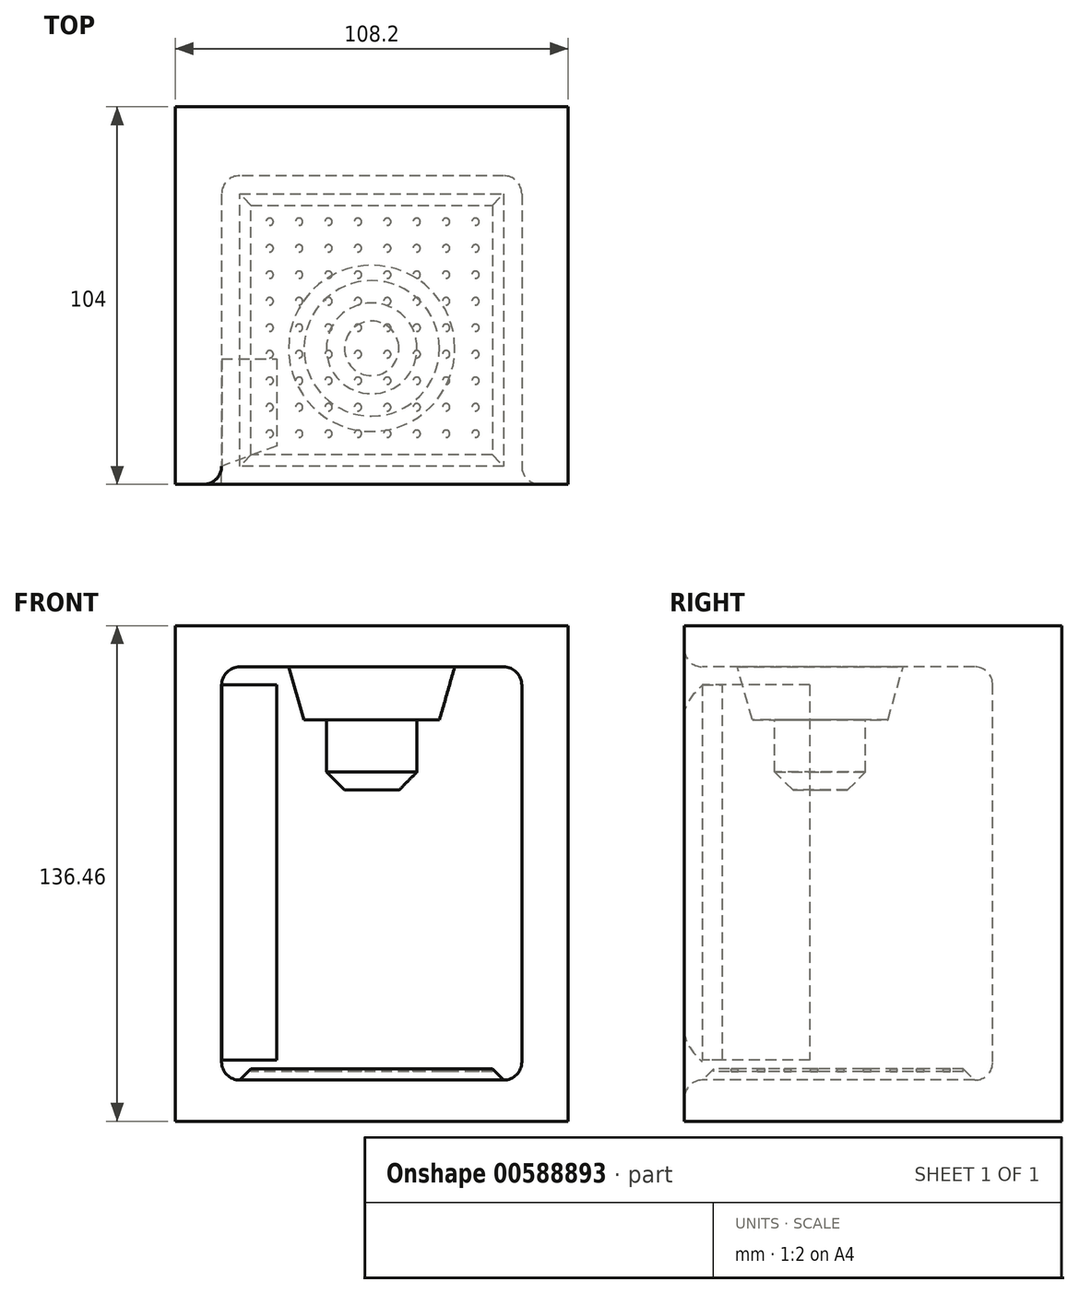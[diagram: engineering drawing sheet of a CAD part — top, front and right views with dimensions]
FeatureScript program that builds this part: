
annotation { "Feature Type Name" : "Feature", "Feature Type Description" : "" }
export const myFeature = defineFeature(function(context is Context, id is Id, definition is map)
    precondition{}
    {
        {
            var Q0;
            Q0=qCreatedBy(makeId("Front.planeOp"),FACE);
            var sketch = newSketch(context, id + "F0", { "sketchPlane" : qUnion([Q0])});
            skLineSegment(sketch, "E0.bottom", {"start": v(54.1, -68.23) * mm, "end": v(-54.1, -68.23) * mm});
            skLineSegment(sketch, "E0.top", {"start": v(54.1, 68.23) * mm, "end": v(-54.1, 68.23) * mm});
            skLineSegment(sketch, "E0.left", {"start": v(54.1, -68.23) * mm, "end": v(54.1, 68.23) * mm});
            skLineSegment(sketch, "E0.right", {"start": v(-54.1, -68.23) * mm, "end": v(-54.1, 68.23) * mm});
            skPoint(sketch, "E0.middle", {"position": v(0, 0) * mm});
            skSolve(sketch);
        }
        {
            var Q0;
            Q0=makeQuery(id+"F0.imprint","IMPRINT",FACE,{"disambiguationData":[TD([[makeQuery(id+"F0.imprint","IMPRINT",EDGE,{"derivedFrom":sQuery(id+"F0.wireOp",EDGE,"E0.bottom")}),-1.0]])]});
            extrude(context, id + "F1", {"entities" : qUnion([Q0]), "depth" : 104 * mm, "offsetDistance" : 25 * mm, "symmetric" : true});
        }
        {
            var Q0;
            Q0=makeQuery(id+"F1.opExtrude","CAP_FACE",FACE,{"disambiguationData":[OSD([sQuery(id+"F0.wireOp",EDGE,"E0.bottom"),sQuery(id+"F0.wireOp",EDGE,"E0.top"),sQuery(id+"F0.wireOp",EDGE,"E0.left"),sQuery(id+"F0.wireOp",EDGE,"E0.right")])],"isStart":false});
            var sketch = newSketch(context, id + "F2", { "sketchPlane" : qUnion([Q0])});
            skLineSegment(sketch, "E1.bottom", {"start": v(41.35, -56.91) * mm, "end": v(-41.35, -56.91) * mm});
            skLineSegment(sketch, "E1.top", {"start": v(41.35, 56.91) * mm, "end": v(-41.35, 56.91) * mm});
            skLineSegment(sketch, "E1.left", {"start": v(41.35, -56.91) * mm, "end": v(41.35, 56.91) * mm});
            skLineSegment(sketch, "E1.right", {"start": v(-41.35, -56.91) * mm, "end": v(-41.35, 56.91) * mm});
            skPoint(sketch, "E1.middle", {"position": v(0, 0) * mm});
            skSolve(sketch);
        }
        {
            var Q0;
            Q0=makeQuery(id+"F2.imprint","IMPRINT",FACE,{"disambiguationData":[TD([[makeQuery(id+"F2.imprint","IMPRINT",EDGE,{"derivedFrom":sQuery(id+"F2.wireOp",EDGE,"E1.bottom")}),-1.0]])]});
            extrude(context, id + "F3", {"entities" : qUnion([Q0]), "operationType" : NewBodyOperationType.REMOVE, "oppositeDirection" : true, "depth" : 85 * mm, "offsetDistance" : 25 * mm});
        }
        {
            var Q0;
            Q0=makeQuery(id+"F3.boolean.opBoolean","COPY",FACE,{"derivedFrom":makeQuery(id+"F3.opExtrude","SWEPT_FACE",FACE,{"disambiguationData":[OSD([sQuery(id+"F2.wireOp",EDGE,"E1.top")])]})});
            var Q1;
            Q1=makeQuery(id+"F3.boolean.opBoolean","COPY",FACE,{"derivedFrom":makeQuery(id+"F3.opExtrude","SWEPT_FACE",FACE,{"disambiguationData":[OSD([sQuery(id+"F2.wireOp",EDGE,"E1.bottom")])]})});
            var Q2;
            Q2=makeQuery(id+"F3.boolean.opBoolean","COPY",FACE,{"derivedFrom":makeQuery(id+"F3.opExtrude","SWEPT_FACE",FACE,{"disambiguationData":[OSD([sQuery(id+"F2.wireOp",EDGE,"E1.left")])]})});
            var Q3;
            Q3=makeQuery(id+"F3.boolean.opBoolean","COPY",FACE,{"derivedFrom":makeQuery(id+"F3.opExtrude","CAP_FACE",FACE,{"disambiguationData":[OSD([sQuery(id+"F2.wireOp",EDGE,"E1.bottom"),sQuery(id+"F2.wireOp",EDGE,"E1.top"),sQuery(id+"F2.wireOp",EDGE,"E1.left"),sQuery(id+"F2.wireOp",EDGE,"E1.right")])],"isStart":false})});
            fillet(context, id + "F4", {"entities" : qUnion([Q0, Q1, Q2, Q3]), "radius" : 5 * mm, "tangentPropagation" : true, "allowEdgeOverflow" : false});
        }
        {
            var Q0;
            Q0=qCreatedBy(makeId("Right.planeOp"),FACE);
            var sketch = newSketch(context, id + "F5", { "sketchPlane" : qUnion([Q0])});
            skLineSegment(sketch, "E2", {"start": v(-14.56, 56.98) * mm, "end": v(-14.56, 35.68) * mm});
            skLineSegment(sketch, "E3", {"start": v(-14.56, 35.68) * mm, "end": v(-2.06, 35.68) * mm});
            skLineSegment(sketch, "E4", {"start": v(-2.06, 35.68) * mm, "end": v(-2.06, 42.37) * mm});
            skLineSegment(sketch, "E5", {"start": v(-2.06, 42.37) * mm, "end": v(4.1, 42.37) * mm});
            skLineSegment(sketch, "E6", {"start": v(4.1, 42.37) * mm, "end": v(8.33, 56.98) * mm});
            skLineSegment(sketch, "E7", {"start": v(8.33, 56.98) * mm, "end": v(-14.56, 56.98) * mm});
            skSolve(sketch);
        }
        {
            var Q0;
            Q0=makeQuery(id+"F5.imprint","IMPRINT",FACE,{"disambiguationData":[TD([[makeQuery(id+"F5.imprint","IMPRINT",EDGE,{"derivedFrom":sQuery(id+"F5.wireOp",EDGE,"E2")}),1.0]])]});
            var Q1;
            Q1=sQuery(id+"F5.wireOp",EDGE,"E2");
            revolve(context, id + "F6", {"entities" : qUnion([Q0]), "axis" : qUnion([Q1]), "revolveType" : RevolveType.FULL});
        }
        {
            var Q0;
            Q0=qCreatedBy(makeId("Front.planeOp"),FACE);
            cPlane(context, id + "F7", {"entities" : qUnion([Q0]), "cplaneType" : CPlaneType.OFFSET, "offset" : 47 * mm, "width" : 150 * mm, "height" : 150 * mm});
        }
        {
            var Q0;
            Q0=qCreatedBy(id+"F7.planeOp",FACE);
            var sketch = newSketch(context, id + "F8", { "sketchPlane" : qUnion([Q0])});
            skLineSegment(sketch, "E8.bottom", {"start": v(-41.3, 51.96) * mm, "end": v(-26.2, 51.96) * mm});
            skLineSegment(sketch, "E8.top", {"start": v(-41.3, -51.37) * mm, "end": v(-26.2, -51.37) * mm});
            skLineSegment(sketch, "E8.left", {"start": v(-41.3, 51.96) * mm, "end": v(-41.3, -51.37) * mm});
            skLineSegment(sketch, "E8.right", {"start": v(-26.2, 51.96) * mm, "end": v(-26.2, -51.37) * mm});
            skSolve(sketch);
        }
        {
            var Q0;
            Q0=makeQuery(id+"F8.imprint","IMPRINT",FACE,{"disambiguationData":[TD([[makeQuery(id+"F8.imprint","IMPRINT",EDGE,{"derivedFrom":sQuery(id+"F8.wireOp",EDGE,"E8.bottom")}),-1.0]])]});
            extrude(context, id + "F9", {"entities" : qUnion([Q0]), "oppositeDirection" : true, "depth" : 29.6 * mm, "offsetDistance" : 25 * mm});
        }
        {
            var Q0;
            Q0=makeQuery(id+"F9.opExtrude","SWEPT_FACE",FACE,{"disambiguationData":[OSD([sQuery(id+"F8.wireOp",EDGE,"E8.bottom")])]});
            var sketch = newSketch(context, id + "F10", { "sketchPlane" : qUnion([Q0])});
            skLineSegment(sketch, "E9", {"start": v(-41.3, -47) * mm, "end": v(-23.88, -40.54) * mm});
            skLineSegment(sketch, "E10", {"start": v(-23.88, -40.54) * mm, "end": v(-23.88, -62.45) * mm});
            skLineSegment(sketch, "E11", {"start": v(-23.88, -62.45) * mm, "end": v(-41.3, -47) * mm});
            skSolve(sketch);
        }
        {
            var Q0;
            {var subQ1=sQuery(id+"F8.wireOp",EDGE,"E8.bottom");var subQ2=makeQuery(id+"F9.opExtrude","CAP_EDGE",EDGE,{"disambiguationData":[OSD([subQ1])],"isStart":true});Q0=makeQuery(id+"F10.imprint","IMPRINT",FACE,{"disambiguationData":[TD([[makeQuery(id+"F10.imprint","IMPRINT",EDGE,{"derivedFrom":subQ2}),1.0]])]});}
            extrude(context, id + "F11", {"entities" : qUnion([Q0]), "operationType" : NewBodyOperationType.REMOVE, "oppositeDirection" : true, "depth" : 104.4 * mm, "offsetDistance" : 25 * mm});
        }
        {
            var Q0;
            Q0=makeQuery(id+"F6.opRevolve","SWEPT_FACE",FACE,{"disambiguationData":[OSD([sQuery(id+"F5.wireOp",EDGE,"E3")])]});
            extrude(context, id + "F12", {"entities" : qUnion([Q0]), "operationType" : NewBodyOperationType.ADD, "depth" : 12.7 * mm, "offsetDistance" : 25 * mm});
        }
        {
            var Q0;
            Q0=makeQuery(id+"F12.opExtrude","CAP_EDGE",EDGE,{"disambiguationData":[OSD([sQuery(id+"F5.wireOp",EDGE,"E3"),sQuery(id+"F5.wireOp",EDGE,"E4")])],"isStart":false});
            chamfer(context, id + "F13", {"entities" : qUnion([Q0]), "width" : 5 * mm, "tangentPropagation" : true});
        }
        {
            var Q0;
            Q0=makeQuery(id+"F3.boolean.opBoolean","COPY",FACE,{"derivedFrom":makeQuery(id+"F3.opExtrude","SWEPT_FACE",FACE,{"disambiguationData":[OSD([sQuery(id+"F2.wireOp",EDGE,"E1.bottom")])]})});
            extrude(context, id + "F14", {"entities" : qUnion([Q0]), "depth" : 3.1 * mm, "offsetDistance" : 25 * mm, "hasDraft" : true, "draftAngle" : 45 * degree, "draftPullDirection" : true});
        }
        {
            var Q0;
            Q0=makeQuery(id+"F14.opExtrude","CAP_FACE",FACE,{"disambiguationData":[OSD([sQuery(id+"F2.wireOp",EDGE,"E1.bottom")])],"isStart":false});
            var sketch = newSketch(context, id + "F15", { "sketchPlane" : qUnion([Q0])});
            skCircle(sketch, "E12", {"center": v(-28.1, 20.32) * mm, "radius": 1 * mm});
            skCircle(sketch, "E13.0.1.0", {"center": v(-28.1, 13.02) * mm, "radius": 1 * mm});
            skCircle(sketch, "E13.0.2.0", {"center": v(-28.1, 5.72) * mm, "radius": 1 * mm});
            skCircle(sketch, "E13.0.3.0", {"center": v(-28.1, -1.58) * mm, "radius": 1 * mm});
            skCircle(sketch, "E13.0.4.0", {"center": v(-28.1, -8.88) * mm, "radius": 1 * mm});
            skCircle(sketch, "E13.0.5.0", {"center": v(-28.1, -16.18) * mm, "radius": 1 * mm});
            skCircle(sketch, "E13.0.6.0", {"center": v(-28.1, -23.48) * mm, "radius": 1 * mm});
            skCircle(sketch, "E13.0.7.0", {"center": v(-28.1, -30.78) * mm, "radius": 1 * mm});
            skCircle(sketch, "E13.0.8.0", {"center": v(-28.1, -38.08) * mm, "radius": 1 * mm});
            skCircle(sketch, "E13.1.0.0", {"center": v(-20, 20.32) * mm, "radius": 1 * mm});
            skCircle(sketch, "E13.1.1.0", {"center": v(-20, 13.02) * mm, "radius": 1 * mm});
            skCircle(sketch, "E13.1.2.0", {"center": v(-20, 5.72) * mm, "radius": 1 * mm});
            skCircle(sketch, "E13.1.3.0", {"center": v(-20, -1.58) * mm, "radius": 1 * mm});
            skCircle(sketch, "E13.1.4.0", {"center": v(-20, -8.88) * mm, "radius": 1 * mm});
            skCircle(sketch, "E13.1.5.0", {"center": v(-20, -16.18) * mm, "radius": 1 * mm});
            skCircle(sketch, "E13.1.6.0", {"center": v(-20, -23.48) * mm, "radius": 1 * mm});
            skCircle(sketch, "E13.1.7.0", {"center": v(-20, -30.78) * mm, "radius": 1 * mm});
            skCircle(sketch, "E13.1.8.0", {"center": v(-20, -38.08) * mm, "radius": 1 * mm});
            skCircle(sketch, "E13.2.0.0", {"center": v(-11.9, 20.32) * mm, "radius": 1 * mm});
            skCircle(sketch, "E13.2.1.0", {"center": v(-11.9, 13.02) * mm, "radius": 1 * mm});
            skCircle(sketch, "E13.2.2.0", {"center": v(-11.9, 5.72) * mm, "radius": 1 * mm});
            skCircle(sketch, "E13.2.3.0", {"center": v(-11.9, -1.58) * mm, "radius": 1 * mm});
            skCircle(sketch, "E13.2.4.0", {"center": v(-11.9, -8.88) * mm, "radius": 1 * mm});
            skCircle(sketch, "E13.2.5.0", {"center": v(-11.9, -16.18) * mm, "radius": 1 * mm});
            skCircle(sketch, "E13.2.6.0", {"center": v(-11.9, -23.48) * mm, "radius": 1 * mm});
            skCircle(sketch, "E13.2.7.0", {"center": v(-11.9, -30.78) * mm, "radius": 1 * mm});
            skCircle(sketch, "E13.2.8.0", {"center": v(-11.9, -38.08) * mm, "radius": 1 * mm});
            skCircle(sketch, "E13.3.0.0", {"center": v(-3.8, 20.32) * mm, "radius": 1 * mm});
            skCircle(sketch, "E13.3.1.0", {"center": v(-3.8, 13.02) * mm, "radius": 1 * mm});
            skCircle(sketch, "E13.3.2.0", {"center": v(-3.8, 5.72) * mm, "radius": 1 * mm});
            skCircle(sketch, "E13.3.3.0", {"center": v(-3.8, -1.58) * mm, "radius": 1 * mm});
            skCircle(sketch, "E13.3.4.0", {"center": v(-3.8, -8.88) * mm, "radius": 1 * mm});
            skCircle(sketch, "E13.3.5.0", {"center": v(-3.8, -16.18) * mm, "radius": 1 * mm});
            skCircle(sketch, "E13.3.6.0", {"center": v(-3.8, -23.48) * mm, "radius": 1 * mm});
            skCircle(sketch, "E13.3.7.0", {"center": v(-3.8, -30.78) * mm, "radius": 1 * mm});
            skCircle(sketch, "E13.3.8.0", {"center": v(-3.8, -38.08) * mm, "radius": 1 * mm});
            skCircle(sketch, "E13.4.0.0", {"center": v(4.3, 20.32) * mm, "radius": 1 * mm});
            skCircle(sketch, "E13.4.1.0", {"center": v(4.3, 13.02) * mm, "radius": 1 * mm});
            skCircle(sketch, "E13.4.2.0", {"center": v(4.3, 5.72) * mm, "radius": 1 * mm});
            skCircle(sketch, "E13.4.3.0", {"center": v(4.3, -1.58) * mm, "radius": 1 * mm});
            skCircle(sketch, "E13.4.4.0", {"center": v(4.3, -8.88) * mm, "radius": 1 * mm});
            skCircle(sketch, "E13.4.5.0", {"center": v(4.3, -16.18) * mm, "radius": 1 * mm});
            skCircle(sketch, "E13.4.6.0", {"center": v(4.3, -23.48) * mm, "radius": 1 * mm});
            skCircle(sketch, "E13.4.7.0", {"center": v(4.3, -30.78) * mm, "radius": 1 * mm});
            skCircle(sketch, "E13.4.8.0", {"center": v(4.3, -38.08) * mm, "radius": 1 * mm});
            skCircle(sketch, "E13.5.0.0", {"center": v(12.4, 20.32) * mm, "radius": 1 * mm});
            skCircle(sketch, "E13.5.1.0", {"center": v(12.4, 13.02) * mm, "radius": 1 * mm});
            skCircle(sketch, "E13.5.2.0", {"center": v(12.4, 5.72) * mm, "radius": 1 * mm});
            skCircle(sketch, "E13.5.3.0", {"center": v(12.4, -1.58) * mm, "radius": 1 * mm});
            skCircle(sketch, "E13.5.4.0", {"center": v(12.4, -8.88) * mm, "radius": 1 * mm});
            skCircle(sketch, "E13.5.5.0", {"center": v(12.4, -16.18) * mm, "radius": 1 * mm});
            skCircle(sketch, "E13.5.6.0", {"center": v(12.4, -23.48) * mm, "radius": 1 * mm});
            skCircle(sketch, "E13.5.7.0", {"center": v(12.4, -30.78) * mm, "radius": 1 * mm});
            skCircle(sketch, "E13.5.8.0", {"center": v(12.4, -38.08) * mm, "radius": 1 * mm});
            skCircle(sketch, "E13.6.0.0", {"center": v(20.5, 20.32) * mm, "radius": 1 * mm});
            skCircle(sketch, "E13.6.1.0", {"center": v(20.5, 13.02) * mm, "radius": 1 * mm});
            skCircle(sketch, "E13.6.2.0", {"center": v(20.5, 5.72) * mm, "radius": 1 * mm});
            skCircle(sketch, "E13.6.3.0", {"center": v(20.5, -1.58) * mm, "radius": 1 * mm});
            skCircle(sketch, "E13.6.4.0", {"center": v(20.5, -8.88) * mm, "radius": 1 * mm});
            skCircle(sketch, "E13.6.5.0", {"center": v(20.5, -16.18) * mm, "radius": 1 * mm});
            skCircle(sketch, "E13.6.6.0", {"center": v(20.5, -23.48) * mm, "radius": 1 * mm});
            skCircle(sketch, "E13.6.7.0", {"center": v(20.5, -30.78) * mm, "radius": 1 * mm});
            skCircle(sketch, "E13.6.8.0", {"center": v(20.5, -38.08) * mm, "radius": 1 * mm});
            skCircle(sketch, "E13.7.0.0", {"center": v(28.6, 20.32) * mm, "radius": 1 * mm});
            skCircle(sketch, "E13.7.1.0", {"center": v(28.6, 13.02) * mm, "radius": 1 * mm});
            skCircle(sketch, "E13.7.2.0", {"center": v(28.6, 5.72) * mm, "radius": 1 * mm});
            skCircle(sketch, "E13.7.3.0", {"center": v(28.6, -1.58) * mm, "radius": 1 * mm});
            skCircle(sketch, "E13.7.4.0", {"center": v(28.6, -8.88) * mm, "radius": 1 * mm});
            skCircle(sketch, "E13.7.5.0", {"center": v(28.6, -16.18) * mm, "radius": 1 * mm});
            skCircle(sketch, "E13.7.6.0", {"center": v(28.6, -23.48) * mm, "radius": 1 * mm});
            skCircle(sketch, "E13.7.7.0", {"center": v(28.6, -30.78) * mm, "radius": 1 * mm});
            skCircle(sketch, "E13.7.8.0", {"center": v(28.6, -38.08) * mm, "radius": 1 * mm});
            skLineSegment(sketch, "E13.direction1", {"start": v(-28.1, 20.32) * mm, "end": v(-20, 20.32) * mm, "construction": true});
            skLineSegment(sketch, "E13.direction2", {"start": v(-28.1, 20.32) * mm, "end": v(-28.1, 13.02) * mm, "construction": true});
            skSolve(sketch);
        }
        {
            var Q0;
            Q0=makeQuery(id+"F15.imprint","IMPRINT",FACE,{"disambiguationData":[TD([[makeQuery(id+"F15.imprint","IMPRINT",EDGE,{"derivedFrom":sQuery(id+"F15.wireOp",EDGE,"E12")}),-1.0]])]});
            extrude(context, id + "F16", {"entities" : qUnion([Q0]), "operationType" : NewBodyOperationType.REMOVE, "oppositeDirection" : true, "depth" : 0.7 * mm, "offsetDistance" : 25 * mm});
        }
    });
